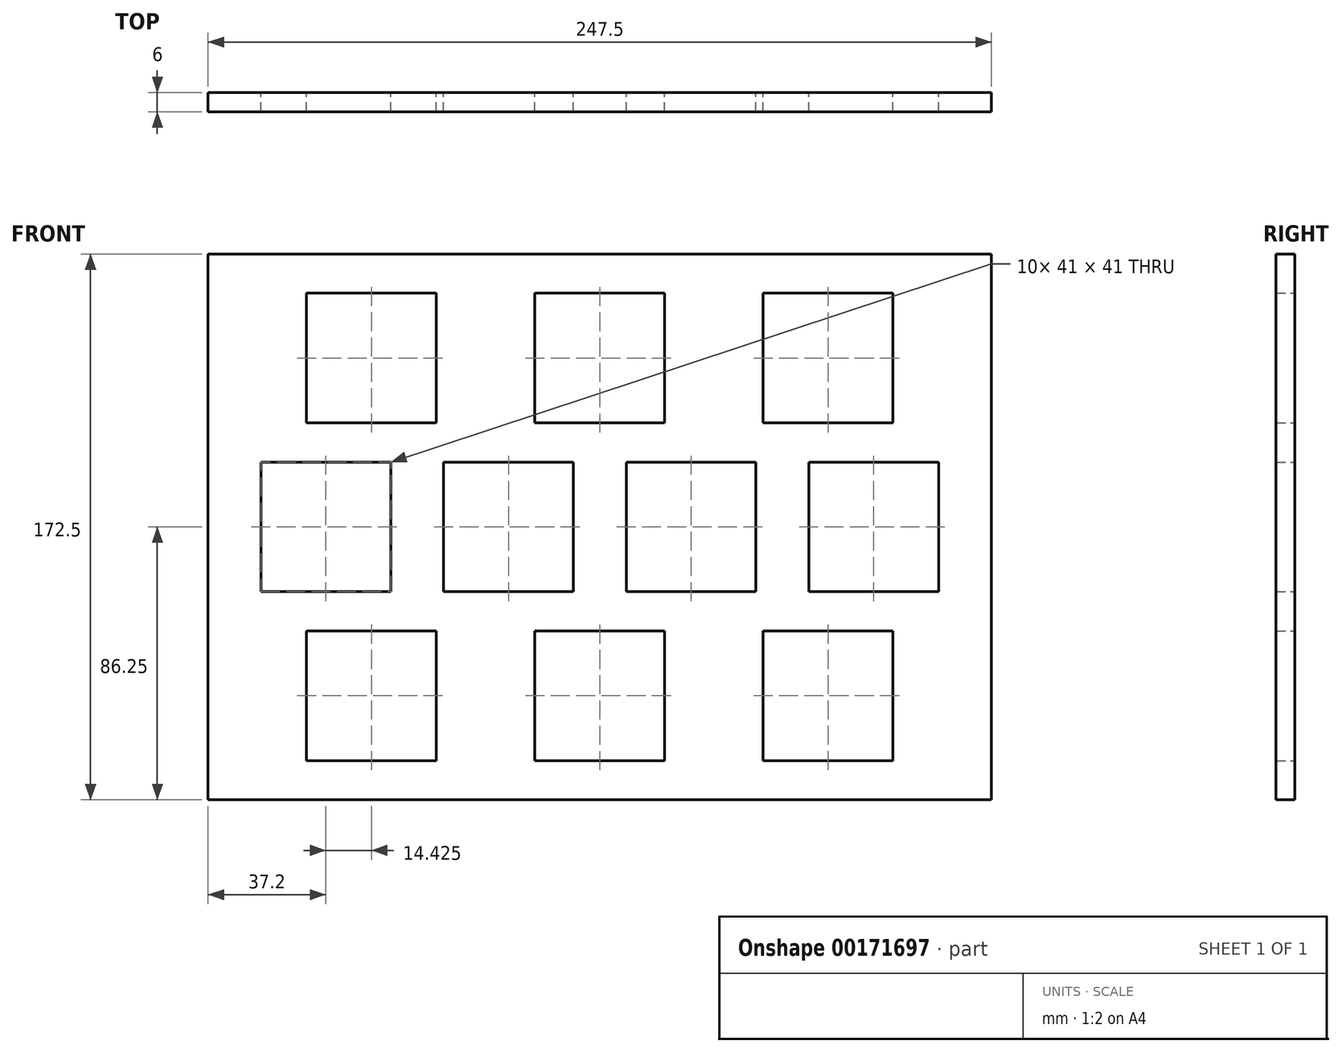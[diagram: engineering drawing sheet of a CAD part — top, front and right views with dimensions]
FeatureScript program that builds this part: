
annotation { "Feature Type Name" : "Feature", "Feature Type Description" : "" }
export const myFeature = defineFeature(function(context is Context, id is Id, definition is map)
    precondition{}
    {
        {
            var Q0;
            Q0=qCreatedBy(makeId("Front.planeOp"),FACE);
            var sketch = newSketch(context, id + "F0", { "sketchPlane" : qUnion([Q0])});
            skLineSegment(sketch, "E0.bottom", {"start": v(123.75, -86.25) * mm, "end": v(-123.75, -86.25) * mm});
            skLineSegment(sketch, "E0.top", {"start": v(123.75, 86.25) * mm, "end": v(-123.75, 86.25) * mm});
            skLineSegment(sketch, "E0.left", {"start": v(123.75, -86.25) * mm, "end": v(123.75, 86.25) * mm});
            skLineSegment(sketch, "E0.right", {"start": v(-123.75, -86.25) * mm, "end": v(-123.75, 86.25) * mm});
            skPoint(sketch, "E0.middle", {"position": v(0, 0) * mm});
            skLineSegment(sketch, "E1.bottom", {"start": v(-66.05, -20.5) * mm, "end": v(-107.05, -20.5) * mm});
            skLineSegment(sketch, "E1.top", {"start": v(-66.05, 20.5) * mm, "end": v(-107.05, 20.5) * mm});
            skLineSegment(sketch, "E1.left", {"start": v(-66.05, -20.5) * mm, "end": v(-66.05, 20.5) * mm});
            skLineSegment(sketch, "E1.right", {"start": v(-107.05, -20.5) * mm, "end": v(-107.05, 20.5) * mm});
            skPoint(sketch, "E1.middle", {"position": v(-86.55, 0) * mm});
            skLineSegment(sketch, "E2.bottom", {"start": v(-51.62, 32.88) * mm, "end": v(-92.62, 32.88) * mm});
            skLineSegment(sketch, "E2.top", {"start": v(-51.62, 73.88) * mm, "end": v(-92.62, 73.88) * mm});
            skLineSegment(sketch, "E2.left", {"start": v(-51.62, 32.88) * mm, "end": v(-51.62, 73.88) * mm});
            skLineSegment(sketch, "E2.right", {"start": v(-92.62, 32.88) * mm, "end": v(-92.62, 73.88) * mm});
            skPoint(sketch, "E2.middle", {"position": v(-72.12, 53.38) * mm});
            skLineSegment(sketch, "E3.0.1.0", {"start": v(-51.62, -32.87) * mm, "end": v(-92.62, -32.87) * mm});
            skLineSegment(sketch, "E3.0.1.1", {"start": v(-51.62, -73.87) * mm, "end": v(-51.62, -32.87) * mm});
            skLineSegment(sketch, "E3.0.1.2", {"start": v(-51.62, -73.87) * mm, "end": v(-92.62, -73.87) * mm});
            skLineSegment(sketch, "E3.0.1.3", {"start": v(-92.62, -73.87) * mm, "end": v(-92.62, -32.87) * mm});
            skLineSegment(sketch, "E3.1.0.0", {"start": v(20.5, 73.88) * mm, "end": v(-20.5, 73.88) * mm});
            skLineSegment(sketch, "E3.1.0.1", {"start": v(20.5, 32.88) * mm, "end": v(20.5, 73.88) * mm});
            skLineSegment(sketch, "E3.1.0.2", {"start": v(20.5, 32.88) * mm, "end": v(-20.5, 32.88) * mm});
            skLineSegment(sketch, "E3.1.0.3", {"start": v(-20.5, 32.88) * mm, "end": v(-20.5, 73.88) * mm});
            skLineSegment(sketch, "E3.1.1.0", {"start": v(20.5, -32.87) * mm, "end": v(-20.5, -32.87) * mm});
            skLineSegment(sketch, "E3.1.1.1", {"start": v(20.5, -73.87) * mm, "end": v(20.5, -32.87) * mm});
            skLineSegment(sketch, "E3.1.1.2", {"start": v(20.5, -73.87) * mm, "end": v(-20.5, -73.87) * mm});
            skLineSegment(sketch, "E3.1.1.3", {"start": v(-20.5, -73.87) * mm, "end": v(-20.5, -32.87) * mm});
            skLineSegment(sketch, "E3.2.0.0", {"start": v(92.62, 73.88) * mm, "end": v(51.62, 73.88) * mm});
            skLineSegment(sketch, "E3.2.0.1", {"start": v(92.62, 32.88) * mm, "end": v(92.62, 73.88) * mm});
            skLineSegment(sketch, "E3.2.0.2", {"start": v(92.63, 32.88) * mm, "end": v(51.63, 32.88) * mm});
            skLineSegment(sketch, "E3.2.0.3", {"start": v(51.63, 32.88) * mm, "end": v(51.62, 73.88) * mm});
            skLineSegment(sketch, "E3.2.1.0", {"start": v(92.62, -32.87) * mm, "end": v(51.62, -32.87) * mm});
            skLineSegment(sketch, "E3.2.1.1", {"start": v(92.62, -73.87) * mm, "end": v(92.62, -32.87) * mm});
            skLineSegment(sketch, "E3.2.1.2", {"start": v(92.63, -73.87) * mm, "end": v(51.63, -73.87) * mm});
            skLineSegment(sketch, "E3.2.1.3", {"start": v(51.63, -73.87) * mm, "end": v(51.62, -32.87) * mm});
            skLineSegment(sketch, "E3.direction1", {"start": v(-92.62, 32.88) * mm, "end": v(-20.5, 32.88) * mm, "construction": true});
            skLineSegment(sketch, "E3.direction2", {"start": v(-92.62, 32.88) * mm, "end": v(-92.62, -73.87) * mm, "construction": true});
            skLineSegment(sketch, "E4.1.0.0", {"start": v(-8.35, 20.5) * mm, "end": v(-49.35, 20.5) * mm});
            skLineSegment(sketch, "E4.1.0.1", {"start": v(-8.35, -20.5) * mm, "end": v(-8.35, 20.5) * mm});
            skLineSegment(sketch, "E4.1.0.2", {"start": v(-8.35, -20.5) * mm, "end": v(-49.35, -20.5) * mm});
            skLineSegment(sketch, "E4.1.0.3", {"start": v(-49.35, -20.5) * mm, "end": v(-49.35, 20.5) * mm});
            skLineSegment(sketch, "E4.2.0.0", {"start": v(49.35, 20.5) * mm, "end": v(8.35, 20.5) * mm});
            skLineSegment(sketch, "E4.2.0.1", {"start": v(49.35, -20.5) * mm, "end": v(49.35, 20.5) * mm});
            skLineSegment(sketch, "E4.2.0.2", {"start": v(49.35, -20.5) * mm, "end": v(8.35, -20.5) * mm});
            skLineSegment(sketch, "E4.2.0.3", {"start": v(8.35, -20.5) * mm, "end": v(8.35, 20.5) * mm});
            skLineSegment(sketch, "E4.3.0.0", {"start": v(107.05, 20.5) * mm, "end": v(66.05, 20.5) * mm});
            skLineSegment(sketch, "E4.3.0.1", {"start": v(107.05, -20.5) * mm, "end": v(107.05, 20.5) * mm});
            skLineSegment(sketch, "E4.3.0.2", {"start": v(107.05, -20.5) * mm, "end": v(66.05, -20.5) * mm});
            skLineSegment(sketch, "E4.3.0.3", {"start": v(66.05, -20.5) * mm, "end": v(66.05, 20.5) * mm});
            skLineSegment(sketch, "E4.direction1", {"start": v(-107.05, -20.5) * mm, "end": v(-49.35, -20.5) * mm, "construction": true});
            skSolve(sketch);
        }
        {
            var Q0;
            Q0 = qSketchRegion(id + "F0", true);
            extrude(context, id + "F1", {"entities" : qUnion([Q0]), "depth" : 6 * mm, "offsetDistance" : 25 * mm});
        }
    });
